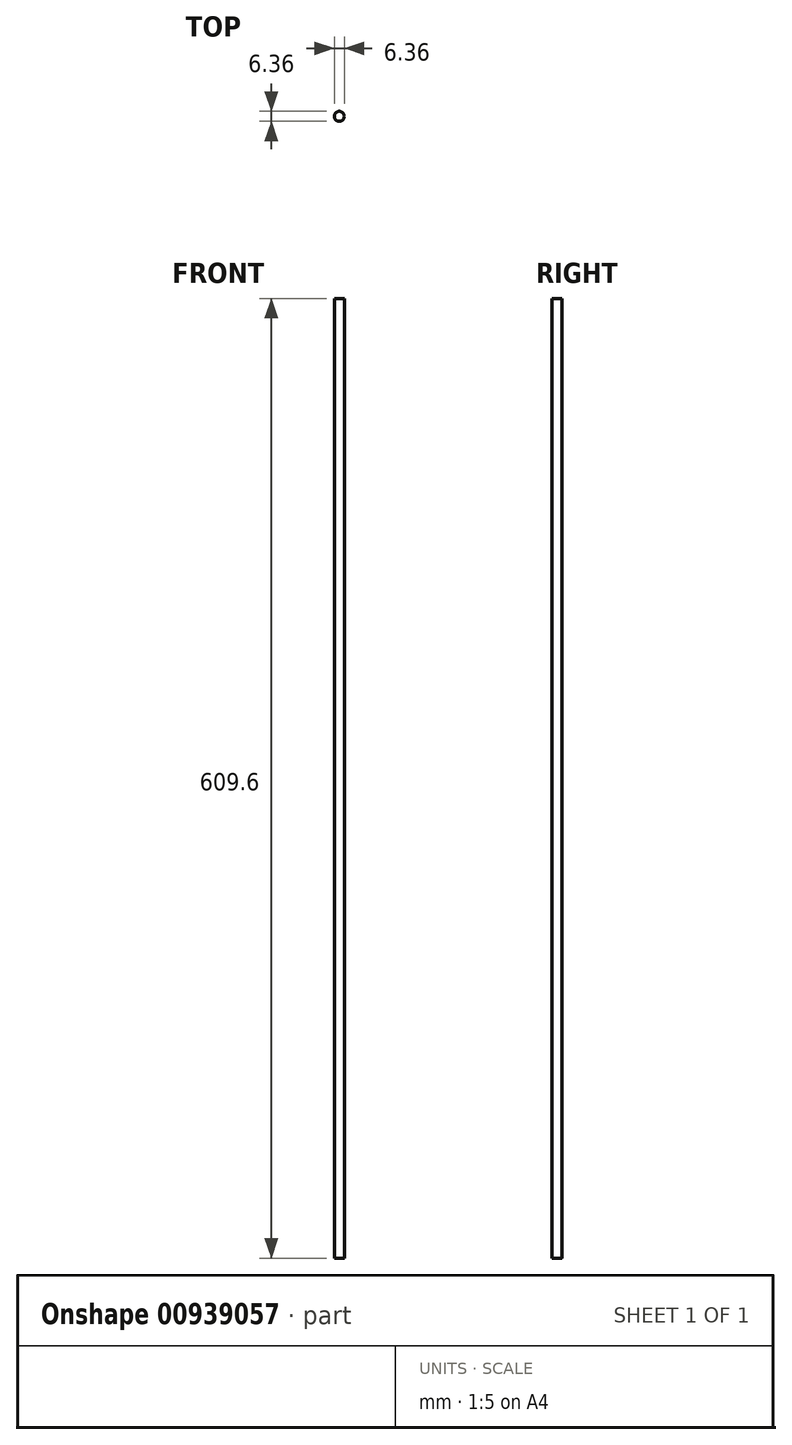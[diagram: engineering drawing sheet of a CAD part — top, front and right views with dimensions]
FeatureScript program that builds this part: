
annotation { "Feature Type Name" : "Feature", "Feature Type Description" : "" }
export const myFeature = defineFeature(function(context is Context, id is Id, definition is map)
    precondition{}
    {
        {
            var Q0;
            Q0=qCreatedBy(makeId("Top.planeOp"),FACE);
            var sketch = newSketch(context, id + "F0", { "sketchPlane" : qUnion([Q0])});
            skCircle(sketch, "E0", {"center": v(0, 0) * mm, "radius": 3.17 * mm});
            skSolve(sketch);
        }
        {
            var Q0;
            Q0 = qSketchRegion(id + "F0", true);
            extrude(context, id + "F1", {"entities" : qUnion([Q0]), "endBound" : BoundingType.SYMMETRIC, "depth" : 609.6 * mm, "offsetDistance" : 25.4 * mm});
        }
    });
